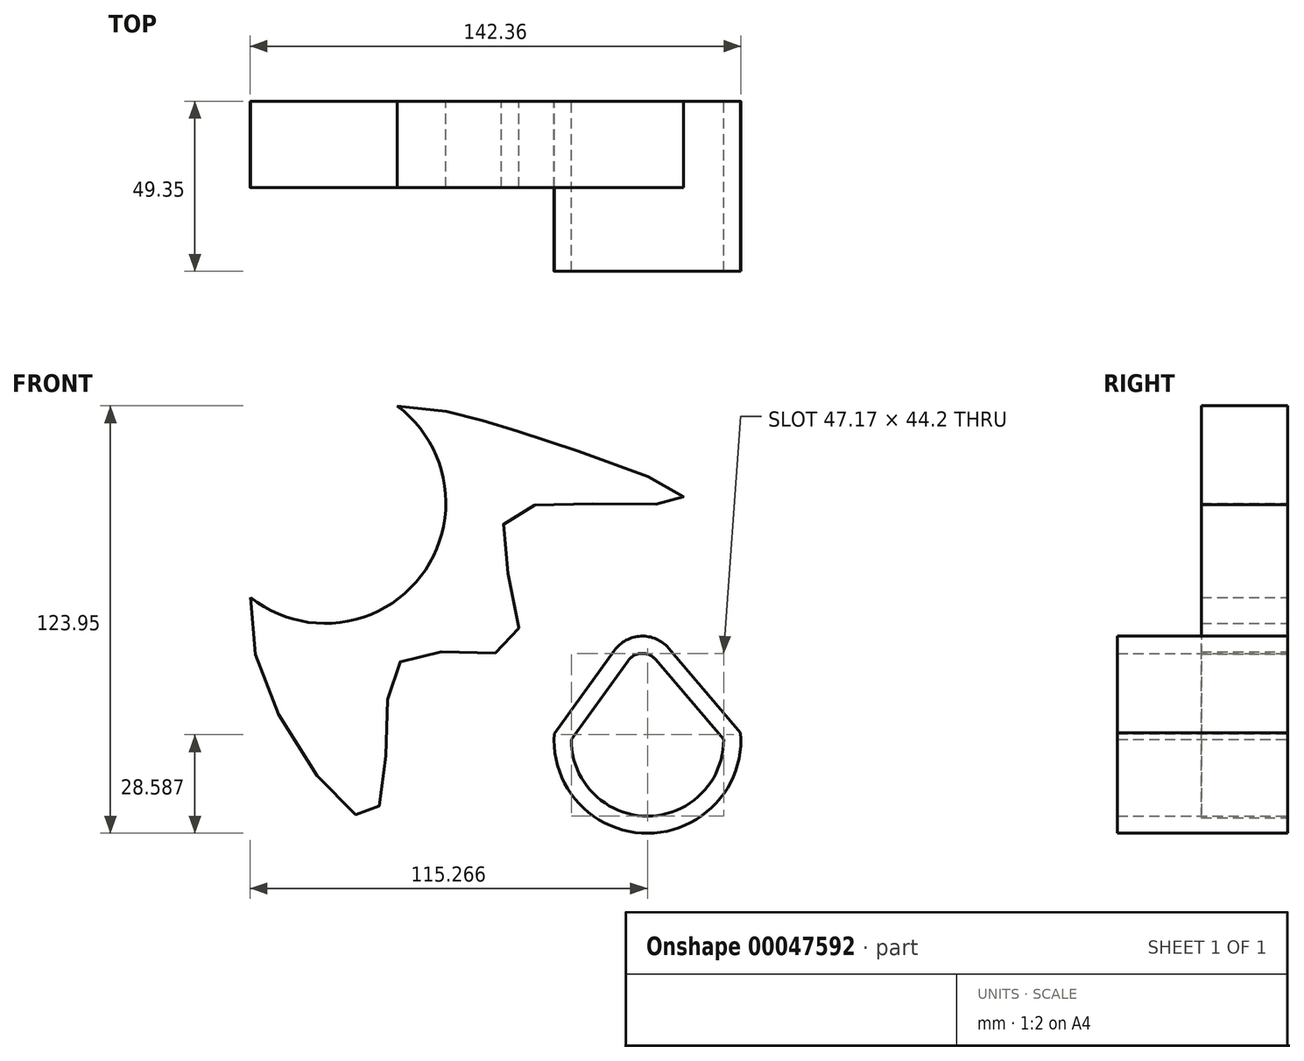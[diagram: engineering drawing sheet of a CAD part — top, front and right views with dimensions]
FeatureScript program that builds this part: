
annotation { "Feature Type Name" : "Feature", "Feature Type Description" : "" }
export const myFeature = defineFeature(function(context is Context, id is Id, definition is map)
    precondition{}
    {
        {
            var Q0;
            Q0=qCreatedBy(makeId("Front.planeOp"),FACE);
            var sketch = newSketch(context, id + "F0", { "sketchPlane" : qUnion([Q0])});
            skLineSegment(sketch, "E0", {"start": v(-0.26, 22.64) * mm, "end": v(-20.02, 45.86) * mm});
            skLineSegment(sketch, "E1", {"start": v(-27.88, 45.55) * mm, "end": v(-44.45, 22.64) * mm});
            skArc(sketch, "E2", {"start": v(-44.45, 22.64) * mm, "mid": v(-22.35, 0.44) * mm, "end": v(-0.26, 22.64) * mm});
            skFitSpline(sketch, "E3", {"points": [v(-130.5, 32.1) * mm, v(-103.02, 0) * mm, v(-98, 27.67) * mm, v(-90.48, 47.33) * mm, v(-60.92, 50.32) * mm, v(-64.5, 83.76) * mm, v(-41.15, 91) * mm, v(-11.94, 93.02) * mm, v(-56.64, 110.95) * mm, v(-74.75, 116.32) * mm, v(-104.82, 117.2) * mm, v(-134.87, 77.18) * mm, v(-130.5, 32.1) * mm]});
            skCircle(sketch, "E4", {"center": v(-115.84, 91.3) * mm, "radius": 35 * mm});
            skPoint(sketch, "E5.visualSharp", {"position": v(-24.15, 50.7) * mm});
            skArc(sketch, "E5.filletArc", {"start": v(-20.02, 45.86) * mm, "mid": v(-24.02, 47.61) * mm, "end": v(-27.88, 45.55) * mm});
            skLineSegment(sketch, "E6", {"start": v(49.15, 62.9) * mm, "end": v(69.64, 16.57) * mm});
            skLineSegment(sketch, "E7", {"start": v(40.56, 40.74) * mm, "end": v(55.84, 47.77) * mm});
            skLineSegment(sketch, "E8", {"start": v(33.42, 54.79) * mm, "end": v(49.15, 62.9) * mm});
            skLineSegment(sketch, "E9", {"start": v(24.84, 71.67) * mm, "end": v(41.53, 80.13) * mm});
            skLineSegment(sketch, "E10", {"start": v(24.84, 71.67) * mm, "end": v(49.16, 23.81) * mm});
            skLineSegment(sketch, "E11", {"start": v(49.15, 62.9) * mm, "end": v(31.52, 75.06) * mm});
            skLineSegment(sketch, "E12.0", {"start": v(4.67, 24.57) * mm, "end": v(-16.21, 49.1) * mm});
            skArc(sketch, "E12.1", {"start": v(-49.4, 24.34) * mm, "mid": v(-22.24, -4.56) * mm, "end": v(4.67, 24.57) * mm});
            skLineSegment(sketch, "E12.2", {"start": v(-31.93, 48.48) * mm, "end": v(-49.4, 24.34) * mm});
            skArc(sketch, "E12.3", {"start": v(-16.21, 49.1) * mm, "mid": v(-24.22, 52.6) * mm, "end": v(-31.93, 48.48) * mm});
            skSolve(sketch);
        }
        {
            var Q0;
            Q0=makeQuery(id+"F0.imprint","IMPRINT",FACE,{"disambiguationData":[TD([[makeQuery(id+"F0.imprint","IMPRINT",EDGE,{"derivedFrom":sQuery(id+"F0.wireOp",EDGE,"E1")}),-1.0]])]});
            extrude(context, id + "F1", {"entities" : qUnion([Q0]), "depth" : 49.35 * mm});
        }
        {
            var Q0;
            {var subQ0=sQuery(id+"F0.wireOp",EDGE,"E4");var subQ1=sQuery(id+"F0.wireOp",EDGE,"E3");var subQ3=makeQuery(id+"F0.imprint","INTERSECT",VERTEX,{"disambiguationData":[OD(0.0)],"derivedFrom":[subQ1,subQ0]});Q0=makeQuery(id+"F0.imprint","IMPRINT",FACE,{"disambiguationData":[TD([[makeQuery(id+"F0.imprint","IMPRINT",EDGE,{"disambiguationData":[TD([[subQ3,-1.0]])],"derivedFrom":subQ1}),1.0]])]});}
            extrude(context, id + "F2", {"entities" : qUnion([Q0]), "depth" : 25 * mm});
        }
        {
            var Q0;
            Q0=makeQuery(id+"F0.imprint","IMPRINT",FACE,{"disambiguationData":[TD([[makeQuery(id+"F0.imprint","IMPRINT",EDGE,{"derivedFrom":sQuery(id+"F0.wireOp",EDGE,"E0")}),-1.0]])]});
            extrude(context, id + "F3", {"entities" : qUnion([Q0]), "operationType" : NewBodyOperationType.ADD, "depth" : 25 * mm});
        }
    });
